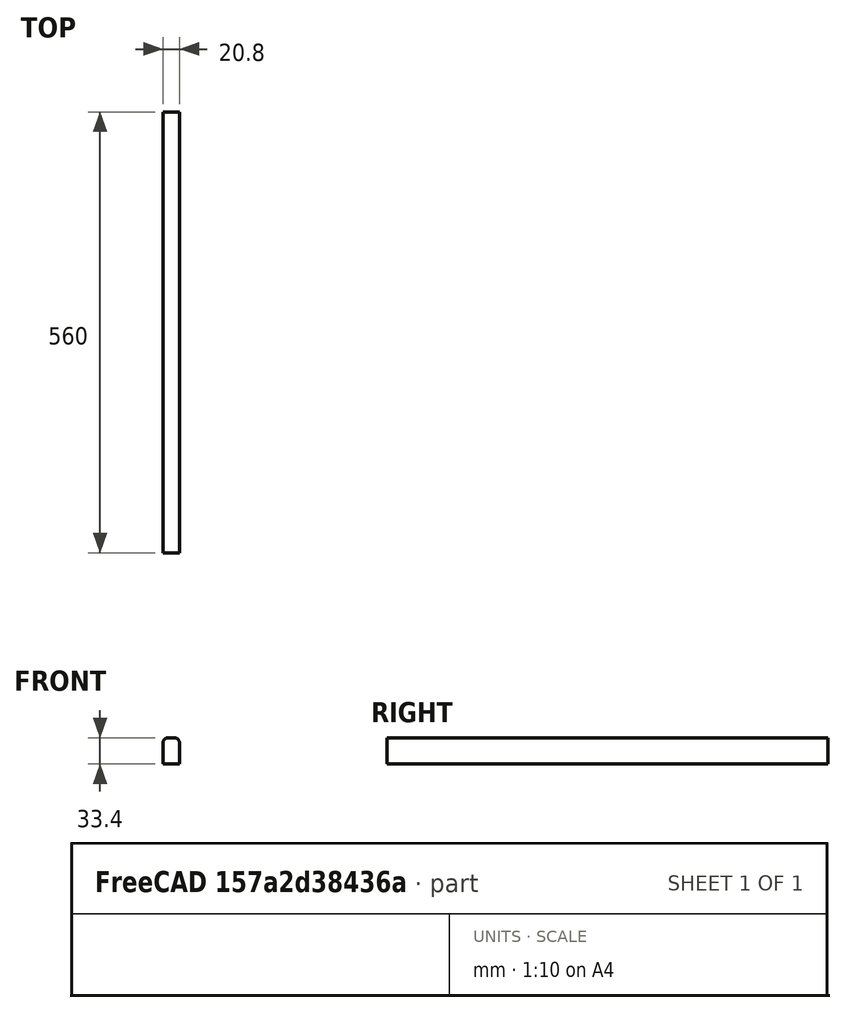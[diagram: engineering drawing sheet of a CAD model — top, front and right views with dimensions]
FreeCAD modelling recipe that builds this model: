
FCSTD DOCUMENT  (FreeCAD 0.21R31527 (Git))
Label: lamp_56_mm
License: All rights reserved
LicenseURL: http://en.wikipedia.org/wiki/All_rights_reserved
objects: Sketcher::SketchObject×1, PartDesign::Pad×1, PartDesign::Body×1
note: 4 computed .brp shape members not serialized (recipe doc carries the construction recipe); baked Part::Feature solids carry a one-line shape summary decoded from their .brp

FEATURE [Sketcher::SketchObject] Sketch
  FullyConstrained = true
  MapMode = 5
  Placement = pos=(0,0,0) rot=(1,0,0;1.5708rad)
  Support = -> [XZ_Plane]
  sketch-geometry (9):
    g0: LineSegment StartX=-10.4 StartY=26.74 StartZ=0 EndX=-10.4 EndY=0 EndZ=0
    g1: LineSegment StartX=-10.4 StartY=0 StartZ=0 EndX=10.4 EndY=0 EndZ=0
    g2: LineSegment StartX=10.4 StartY=0 StartZ=0 EndX=10.4 EndY=26.74 EndZ=0
    g3: LineSegment StartX=3.74 StartY=33.4 StartZ=0 EndX=-3.74 EndY=33.4 EndZ=0
    g4: GeomPoint X=0 Y=16.7 Z=0
    g5: ArcOfCircle CenterX=3.74 CenterY=26.74 CenterZ=0 NormalX=0 NormalY=0 NormalZ=1 AngleXU=0 Radius=6.66 StartAngle=3e-16 EndAngle=1.5708
    g6: GeomPoint X=10.4 Y=33.4 Z=0
    g7: ArcOfCircle CenterX=-3.74 CenterY=26.74 CenterZ=0 NormalX=0 NormalY=0 NormalZ=1 AngleXU=0 Radius=6.66 StartAngle=1.5708 EndAngle=3.14159
    g8: GeomPoint X=-10.4 Y=33.4 Z=0
  constraints (21):
    c: Coincident(g0,g1)
    c: Coincident(g1,g2)
    c: Horizontal(g1)
    c: Horizontal(g3)
    c: Vertical(g0)
    c: Vertical(g2)
    c: Symmetric(g1,g8,g4)
    c: PointOnObject(g4,g-2)
    c: PointOnObject(g1,g-1)
    c: DistanceX(g0,g1) = 20.8
    c: DistanceY(g6) = 33.4
    c: PointOnObject(g6,g3)
    c: PointOnObject(g6,g2)
    c: Tangent(g3,g5) = -1.5708
    c: Tangent(g2,g5) = -1.5708
    c: PointOnObject(g8,g0)
    c: PointOnObject(g8,g3)
    c: Tangent(g0,g7) = -1.5708
    c: Tangent(g3,g7) = -1.5708
    c: Equal(g5,g7)
    c: Diameter(g5) = 13.32
FEATURE [PartDesign::Pad] Pad
  Direction = (0,-1,2e-16)
  Length = 560
  Length2 = 10
  Placement = pos=(0,0,0) rot=(1,0,0;1.5708rad)
  Profile = -> Sketch
  ReferenceAxis = -> Sketch [N_Axis]
  Reversed = true
  Type = 0
FEATURE [PartDesign::Body] Body
  Group = -> [Sketch,Pad]
  Origin = -> Origin
  Tip = -> Pad
